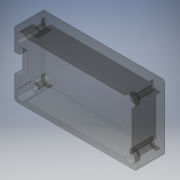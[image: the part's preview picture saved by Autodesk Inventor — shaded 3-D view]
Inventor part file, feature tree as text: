
AUTODESK INVENTOR PART (.ipt)
format: ipt  version: 2019 (Build 230136000, 136)  size: 225,792 bytes
history: native  units: mm
features: extrude x9, sketch x2, fillet x1
ambient origin geometry x8: Origin, YZ Plane, XZ Plane, XY Plane, X Axis, Y Axis, Z Axis, Center Point
bodies: Solid1 (feature_tree)
feature tree (12):
  extrude  "Extrusion1"  Depth=22.75mm
  fillet  "Fillet1"  Radius=5.3mm
  sketch  "Sketch2"  dims[d4=0.5mm d5=0.25mm d6=1.1mm d7=1.0mm d8=3.5mm d9=20.0mm d10=9.0mm d11=1.0mm d12=2.0mm d13=4.5mm d14=0.0mm d15=4.5mm d16=0.0mm d17=2.0mm d18=0.0mm d19=4.5mm d20=0.0mm d21=3.5mm d22=0.0mm d23=4.5mm d24=0.0mm d25=1.5mm d26=0.0mm d27=0.75mm d28=0.0mm]
  extrude  "Extrusion2"  Depth=0.25mm
  extrude  "Extrusion3"  Depth=1.1mm
  extrude  "Extrusion4"  Depth=1.0mm
  extrude  "Extrusion5"  Depth=3.5mm
  extrude  "Extrusion6"  Depth=0.75mm
  extrude  "Extrusion7"  Depth=0.75mm
  extrude  "Extrusion8"  Depth=1.0mm
  extrude  "Extrusion9"  Depth=2.0mm
  sketch  "Sketch1"  dims[d0=12.2mm d1=22.75mm d2=5.3mm d3=0.0mm]
